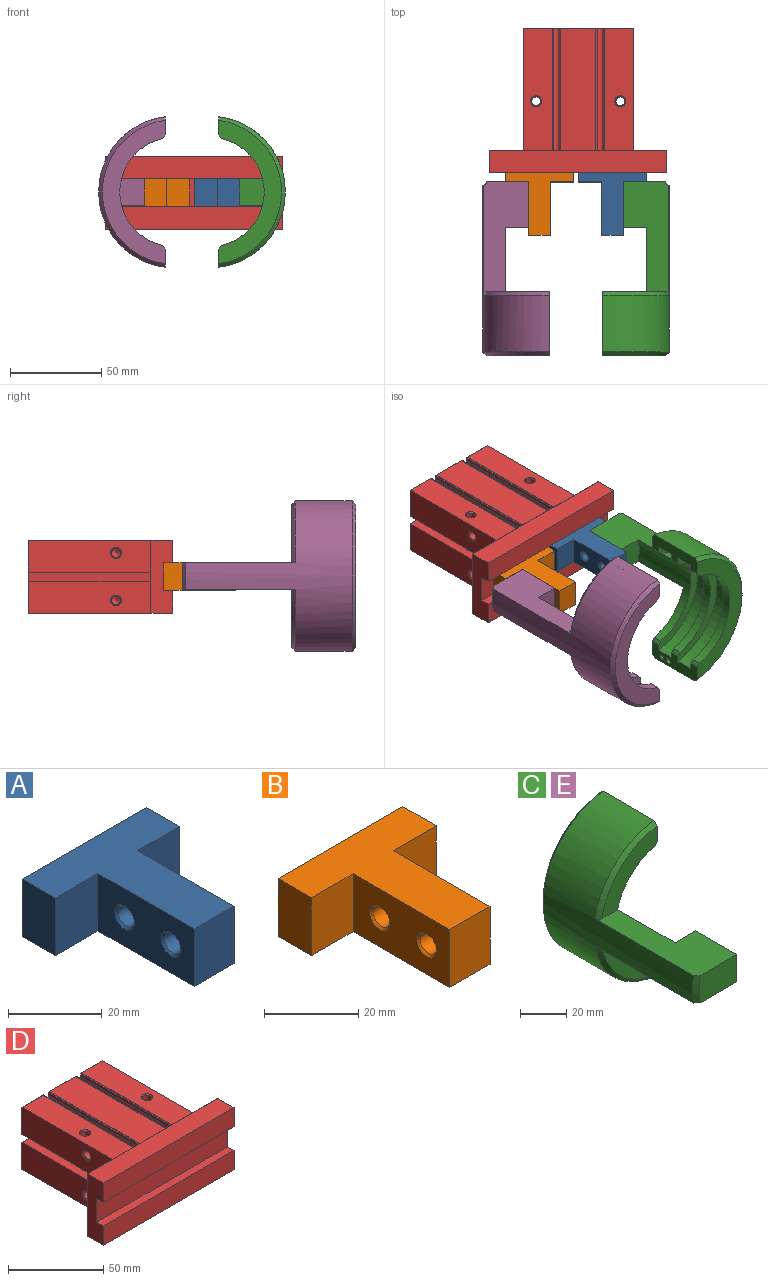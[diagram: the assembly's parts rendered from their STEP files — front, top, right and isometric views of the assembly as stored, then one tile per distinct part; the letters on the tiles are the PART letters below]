
ASSEMBLY  parts=5 mates=10
PART A: 16 faces, bbox 37.4x39x15 mm
  f0: cone r=3.23mm half-angle=45deg, axis (1,0,0), area 13.1mm2, adj f1,f8
  f1: cylinder r=2.46mm len=10.92mm, axis (1,0,0), area 168.8mm2, adj f0,f2
  f2: cone r=3.23mm half-angle=45deg, axis (-1,0,0), area 13.1mm2, adj f1,f6
  f3: cone r=3.23mm half-angle=45deg, axis (1,0,0), area 13.1mm2, adj f4,f8
  f4: cylinder r=2.46mm len=10.92mm, axis (1,0,0), area 168.8mm2, adj f3,f5
  f5: cone r=3.23mm half-angle=45deg, axis (-1,0,0), area 13.1mm2, adj f4,f6
  f6: plane 29x15mm, normal (-1,0,0), area 378.5mm2, adj f2,f5,f7,f13,f14,f15
  f7: plane 15x12mm, normal (0,-1,0), area 180mm2, adj f6,f8,f14,f15
  f8: plane 29x15mm, normal (1,0,0), area 378.5mm2, adj f0,f3,f7,f9,f14,f15
  f9: plane 15x12.5mm, normal (0,-1,0), area 187.5mm2, adj f8,f10,f14,f15
  f10: plane 15x10mm, normal (1,0,0), area 150mm2, adj f9,f11,f14,f15
  f11: plane 37.4x15mm, normal (0,1,0), area 561mm2, adj f10,f12,f14,f15
  f12: plane 15x10mm, normal (-1,0,0), area 150mm2, adj f11,f13,f14,f15
  f13: plane 15x12.9mm, normal (0,-1,0), area 193.5mm2, adj f6,f12,f14,f15
  f14: plane 39x37.4mm, normal (0,0,-1), area 722mm2, adj f6,f7,f8,f9,f10,f11,f12,f13
  f15: plane 39x37.4mm, normal (0,0,1), area 722mm2, adj f6,f7,f8,f9,f10,f11,f12,f13
PART B: 16 faces, bbox 37.4x39x15 mm
  f0: cone r=3.23mm half-angle=45deg, axis (1,0,0), area 13.1mm2, adj f1,f8
  f1: cylinder r=2.46mm len=10.92mm, axis (1,0,0), area 168.8mm2, adj f0,f2
  f2: cone r=3.23mm half-angle=45deg, axis (-1,0,0), area 13.1mm2, adj f1,f6
  f3: cone r=3.23mm half-angle=45deg, axis (1,0,0), area 13.1mm2, adj f4,f8
  f4: cylinder r=2.46mm len=10.92mm, axis (1,0,0), area 168.8mm2, adj f3,f5
  f5: cone r=3.23mm half-angle=45deg, axis (-1,0,0), area 13.1mm2, adj f4,f6
  f6: plane 29x15mm, normal (-1,0,0), area 378.5mm2, adj f2,f5,f7,f13,f14,f15
  f7: plane 15x12mm, normal (0,-1,0), area 180mm2, adj f6,f8,f14,f15
  f8: plane 29x15mm, normal (1,0,0), area 378.5mm2, adj f0,f3,f7,f9,f14,f15
  f9: plane 15x12.9mm, normal (0,-1,0), area 193.5mm2, adj f8,f10,f14,f15
  f10: plane 15x10mm, normal (1,0,0), area 150mm2, adj f9,f11,f14,f15
  f11: plane 37.4x15mm, normal (0,1,0), area 561mm2, adj f10,f12,f14,f15
  f12: plane 15x10mm, normal (-1,0,0), area 150mm2, adj f11,f13,f14,f15
  f13: plane 15x12.5mm, normal (0,-1,0), area 187.5mm2, adj f6,f12,f14,f15
  f14: plane 39x37.4mm, normal (0,0,-1), area 722mm2, adj f6,f7,f8,f9,f10,f11,f12,f13
  f15: plane 39x37.4mm, normal (0,0,1), area 722mm2, adj f6,f7,f8,f9,f10,f11,f12,f13
PART C: 38 faces, bbox 36.7x95x82.4 mm
  f0: plane 25x14.41mm, normal (1,0,0), area 360.3mm2, adj f1,f2,f35,f37
  f1: plane 60.01x24.38mm, normal (0,0,-1), area 1018.4mm2, adj f0,f5,f15,f16,f33,f35,f36,f37
  f2: plane 60.01x24.38mm, normal (0,0,1), area 1018.4mm2, adj f0,f6,f15,f16,f34,f35,f36,f37
  f3: plane 2x1.97mm, normal (0.17,0,0.98), area 2mm2, adj f16,f21,f34
  f4: plane 2x1.97mm, normal (0.17,0,-0.98), area 2mm2, adj f16,f22,f33
  f5: plane 33.84x31.98mm, normal (0,-1,0), area 400.6mm2, adj f1,f8,f15,f19,f22
  f6: plane 33.84x31.98mm, normal (0,-1,0), area 400.6mm2, adj f2,f9,f15,f20,f21
  f7: cylinder r=30mm len=58.55mm, axis (0,1,0), area 405.1mm2, adj f10,f11,f17,f27
  f8: plane 35.01x9.98mm, normal (1,0,0), area 262.6mm2, adj f5,f10,f13,f16,f17,f18,f19,f22
  f9: plane 35.01x9.98mm, normal (1,0,0), area 276.7mm2, adj f6,f11,f14,f16,f17,f18,f20,f21
  f10: plane 5x1.95mm, normal (0.78,0,0.62), area 12.5mm2, adj f7,f8,f17,f27
  f11: plane 5x1.95mm, normal (0.78,0,-0.62), area 12.5mm2, adj f7,f9,f17,f27
  f12: cylinder r=30mm len=58.55mm, axis (0,1,0), area 405.1mm2, adj f13,f14,f24,f28
  f13: plane 5x1.95mm, normal (0.78,0,0.62), area 12.5mm2, adj f8,f12,f24,f28
  f14: plane 5x1.95mm, normal (0.78,0,-0.62), area 12.5mm2, adj f9,f12,f24,f28
  f15: cylinder r=30mm len=58.55mm, axis (0,1,0), area 914.5mm2, adj f1,f2,f5,f6,f19,f20,f25,f37
  f16: cylinder r=41.5mm len=91mm, axis (0,1,0), area 4600.1mm2, adj f1,f2,f3,f4,f8,f9,f18,f21
  f17: plane 78.36x34.5mm, normal (0,1,0), area 939.2mm2, adj f7,f8,f9,f10,f11,f18
  f18: cone r=41.5mm half-angle=45deg, axis (0,-1,0), area 331.5mm2, adj f8,f9,f16,f17
  f19: plane 5x1.95mm, normal (0.78,0,0.62), area 12.5mm2, adj f5,f8,f15,f25
  f20: plane 5x1.95mm, normal (0.78,0,-0.62), area 12.5mm2, adj f6,f9,f15,f25
  f21: cone r=39.5mm half-angle=45deg, axis (0,1,0), area 145.8mm2, adj f3,f6,f9,f16,f34
  f22: cone r=39.5mm half-angle=45deg, axis (0,1,0), area 145.8mm2, adj f4,f5,f8,f16,f33
  f23: cylinder r=35mm len=69.28mm, axis (0,-1,0), area 999.2mm2, adj f8,f9,f24,f25
  f24: plane 69.28x30mm, normal (0,-1,0), area 457.8mm2, adj f8,f9,f12,f13,f14,f23
  f25: plane 69.28x30mm, normal (0,1,0), area 457.8mm2, adj f8,f9,f15,f19,f20,f23
  f26: cylinder r=35mm len=69.28mm, axis (0,-1,0), area 999.2mm2, adj f8,f9,f27,f28
  f27: plane 69.28x30mm, normal (0,-1,0), area 457.8mm2, adj f7,f8,f9,f10,f11,f26
  f28: plane 69.28x30mm, normal (0,1,0), area 457.8mm2, adj f8,f9,f12,f13,f14,f26
  f29: cylinder r=1.5mm len=5mm, axis (1,0,0), area 47.1mm2, adj f8,f30
  f30: plane 3x3mm, normal (1,0,0), area 7.1mm2, adj f29
  f31: cylinder r=1.5mm len=5mm, axis (1,0,0), area 47.1mm2, adj f8,f32
  f32: plane 3x3mm, normal (1,0,0), area 7.1mm2, adj f31
  f33: plane 2.03x0.35mm, normal (0,1,0), area 0.4mm2, adj f1,f4,f22
  f34: plane 2.03x0.35mm, normal (0,1,0), area 0.4mm2, adj f2,f3,f21
  f35: plane 23x14.41mm, normal (0,-1,0), area 328.3mm2, adj f0,f1,f2,f36
  f36: cone r=39.5mm half-angle=45deg, axis (0,1,0), area 41mm2, adj f1,f2,f16,f35
  f37: plane 14.41x13.5mm, normal (0,1,0), area 190.4mm2, adj f0,f1,f2,f15
PART D: 114 faces, bbox 97x79x40 mm
  f0: cylinder r=2.5mm len=5mm, axis (0,-1,0), area 78.5mm2, adj f43,f96
  f1: cone r=1.23mm half-angle=60deg, axis (0,1,0), area 22mm2, adj f2
  f2: cylinder r=2.46mm len=15.46mm, axis (0,-1,0), area 239mm2, adj f1,f3
  f3: cone r=3.23mm half-angle=45deg, axis (0,1,0), area 13.1mm2, adj f2,f43
  f4: cone r=3.23mm half-angle=45deg, axis (0,1,0), area 13.1mm2, adj f5,f43
  f5: cylinder r=2.46mm len=15.46mm, axis (0,1,0), area 239mm2, adj f4,f6
  f6: cone r=1.23mm half-angle=60deg, axis (0,1,0), area 22mm2, adj f5
  f7: cone r=2.87mm half-angle=45deg, axis (1,0,0), area 5.5mm2, adj f8,f46
  f8: cylinder r=2.24mm len=4.74mm, axis (1,0,0), area 66.7mm2, adj f7,f95
  f9: cylinder r=2.24mm len=4.74mm, axis (-1,0,0), area 66.7mm2, adj f10,f94
  f10: cone r=2.87mm half-angle=45deg, axis (1,0,0), area 5.5mm2, adj f9,f46
  f11: cone r=3.23mm half-angle=45deg, axis (0,0,-1), area 13.1mm2, adj f22,f36
  f12: cylinder r=2.46mm len=16.95mm, axis (0,0,-1), area 258.2mm2, adj f13,f54,f55,f56,f60
  f13: cone r=3.23mm half-angle=45deg, axis (0,0,1), area 13.1mm2, adj f12,f50
  f14: cone r=3.23mm half-angle=45deg, axis (0,0,-1), area 13.1mm2, adj f21,f36
  f15: cylinder r=2.46mm len=16.95mm, axis (0,0,-1), area 258.2mm2, adj f16,f45,f63,f67,f68
  f16: cone r=3.23mm half-angle=45deg, axis (0,0,1), area 13.1mm2, adj f15,f50
  f17: cylinder r=2.01mm len=66.8mm, axis (0,-1,0), area 594.2mm2, adj f43,f89,f91,f92
  f18: cylinder r=2.01mm len=66.8mm, axis (0,-1,0), area 594.2mm2, adj f43,f83,f85,f86
  f19: cylinder r=2.01mm len=66.8mm, axis (0,-1,0), area 594.2mm2, adj f43,f78,f80,f81
  f20: cylinder r=2.01mm len=66.8mm, axis (0,-1,0), area 594.2mm2, adj f43,f71,f74,f75
  f21: cylinder r=2.46mm len=16.95mm, axis (0,0,-1), area 258.2mm2, adj f14,f47,f65,f66,f69
  f22: cylinder r=2.46mm len=16.95mm, axis (0,0,-1), area 258.2mm2, adj f11,f57,f58,f59,f61
  f23: cone r=1.23mm half-angle=60deg, axis (-1,0,0), area 22mm2, adj f24
  f24: cylinder r=2.46mm len=10.46mm, axis (1,0,0), area 161.7mm2, adj f23,f25
  f25: cone r=3.23mm half-angle=45deg, axis (-1,0,0), area 13.1mm2, adj f24,f51
  f26: cone r=3.23mm half-angle=45deg, axis (-1,0,0), area 13.1mm2, adj f27,f51
  f27: cylinder r=2.46mm len=10.46mm, axis (-1,0,0), area 161.7mm2, adj f26,f28
  f28: cone r=1.23mm half-angle=60deg, axis (-1,0,0), area 22mm2, adj f27
  f29: cylinder r=17mm len=34mm, axis (0,-1,0), area 427.3mm2, adj f43,f52
  f30: plane 19.3x0.09mm, normal (0,0.71,-0.71), area 2.5mm2, adj f35,f36,f43,f73
  f31: plane 15.65x0.09mm, normal (0,0.71,-0.71), area 2mm2, adj f34,f36,f43,f48
  f32: plane 15.65x0.09mm, normal (0,0.71,-0.71), area 2mm2, adj f33,f36,f43,f77
  f33: plane 17.49x0.09mm, normal (0.71,0.71,0), area 2.2mm2, adj f32,f43,f46,f47
  f34: plane 66.8x0.21mm, normal (1,0,0), area 14mm2, adj f31,f36,f43,f79,f80
  f35: plane 66.8x0.21mm, normal (-1,0,0), area 14mm2, adj f30,f36,f43,f80,f82
  f36: plane 66.91x60mm, normal (0,0,-1), area 3331mm2, adj f11,f14,f30,f31,f32,f34,f35,f46
  f37: plane 19.3x0.09mm, normal (0,0.71,0.71), area 2.5mm2, adj f42,f43,f50,f88
  f38: plane 15.65x0.09mm, normal (0,0.71,0.71), area 2mm2, adj f41,f43,f49,f50
  f39: plane 15.65x0.09mm, normal (0,0.71,0.71), area 2mm2, adj f40,f43,f44,f50
  f40: plane 66.8x0.21mm, normal (-1,0,0), area 14mm2, adj f39,f43,f50,f84,f85
  f41: plane 66.8x0.21mm, normal (1,0,0), area 14mm2, adj f38,f43,f50,f91,f93
  f42: plane 66.8x0.21mm, normal (-1,0,0), area 14mm2, adj f37,f43,f50,f90,f91
  f43: plane 59.82x39.82mm, normal (0,1,0), area 1204.2mm2, adj f0,f3,f4,f17,f18,f19,f20,f29
  f44: plane 17.49x0.09mm, normal (0.71,0.71,0), area 2.2mm2, adj f39,f43,f45,f46
  f45: plane 66.8x7.7mm, normal (0,0,-1), area 501.5mm2, adj f15,f43,f44,f46,f63,f68,f70
  f46: plane 66.91x40mm, normal (1,0,0), area 2302.2mm2, adj f7,f10,f33,f36,f44,f45,f47,f50
  f47: plane 66.8x7.7mm, normal (0,0,1), area 501.5mm2, adj f21,f33,f43,f46,f66,f69,f70
  f48: plane 17.49x0.09mm, normal (-0.71,0.71,0), area 2.2mm2, adj f31,f43,f51,f61
  f49: plane 17.49x0.09mm, normal (-0.71,0.71,0), area 2.2mm2, adj f38,f43,f51,f60
  f50: plane 66.91x60mm, normal (0,0,1), area 3331mm2, adj f13,f16,f37,f38,f39,f40,f41,f42
  f51: plane 66.91x40mm, normal (-1,0,0), area 2285mm2, adj f25,f26,f36,f48,f49,f50,f60,f61
  f52: plane 34x34mm, normal (0,1,0), area 907.9mm2, adj f29
  f53: plane 66.8x6.22mm, normal (-1,0,0), area 415.5mm2, adj f43,f54,f59,f62
  f54: plane 66.8x3.8mm, normal (0,0,-1), area 247.8mm2, adj f12,f43,f53,f55,f56,f62
  f55: plane 24.44x0.6mm, normal (1,0,0), area 14.7mm2, adj f12,f54,f60,f62
  f56: plane 37.64x0.6mm, normal (1,0,0), area 22.6mm2, adj f12,f43,f54,f60
  f57: plane 24.44x0.6mm, normal (1,0,0), area 14.7mm2, adj f22,f59,f61,f62
  f58: plane 37.64x0.6mm, normal (1,0,0), area 22.6mm2, adj f22,f43,f59,f61
  f59: plane 66.8x3.8mm, normal (0,0,1), area 247.8mm2, adj f22,f43,f53,f57,f58,f62
  f60: plane 66.8x7.7mm, normal (0,0,-1), area 501.4mm2, adj f12,f43,f49,f51,f55,f56,f62
  f61: plane 66.8x7.7mm, normal (0,0,1), area 501.4mm2, adj f22,f43,f48,f51,f57,f58,f62
  f62: plane 11.5x6.22mm, normal (0,1,0), area 62.3mm2, adj f51,f53,f54,f55,f57,f59,f60,f61
  f63: plane 24.44x0.6mm, normal (-1,0,0), area 14.7mm2, adj f15,f45,f67,f70
  f64: plane 66.8x6.22mm, normal (1,0,0), area 415.5mm2, adj f43,f65,f67,f70
  f65: plane 66.8x3.8mm, normal (0,0,1), area 247.7mm2, adj f21,f43,f64,f66,f69,f70
  f66: plane 24.44x0.6mm, normal (-1,0,0), area 14.7mm2, adj f21,f47,f65,f70
  f67: plane 66.8x3.8mm, normal (0,0,-1), area 247.7mm2, adj f15,f43,f63,f64,f68,f70
  f68: plane 37.64x0.6mm, normal (-1,0,0), area 22.6mm2, adj f15,f43,f45,f67
  f69: plane 37.64x0.6mm, normal (-1,0,0), area 22.6mm2, adj f21,f43,f47,f65
  f70: plane 11.5x6.22mm, normal (0,1,0), area 62.3mm2, adj f45,f46,f47,f63,f64,f65,f66,f67
  f71: plane 66.8x1.89mm, normal (1,0,0), area 126mm2, adj f20,f43,f72,f74
  f72: plane 66.8x0.74mm, normal (0,0,-1), area 49.4mm2, adj f43,f71,f73,f74
  f73: plane 66.8x0.21mm, normal (1,0,0), area 14mm2, adj f30,f36,f43,f72,f74
  f74: plane 5.31x4.7mm, normal (0,1,0), area 17.9mm2, adj f20,f36,f71,f72,f73,f75,f76,f77
  f75: plane 66.8x1.89mm, normal (-1,0,0), area 126mm2, adj f20,f43,f74,f76
  f76: plane 66.8x0.74mm, normal (0,0,-1), area 49.4mm2, adj f43,f74,f75,f77
  f77: plane 66.8x0.21mm, normal (-1,0,0), area 14mm2, adj f32,f36,f43,f74,f76
  f78: plane 66.8x1.89mm, normal (1,0,0), area 126mm2, adj f19,f43,f79,f80
  f79: plane 66.8x0.74mm, normal (0,0,-1), area 49.4mm2, adj f34,f43,f78,f80
  f80: plane 5.31x4.7mm, normal (0,1,0), area 17.9mm2, adj f19,f34,f35,f36,f78,f79,f81,f82
  f81: plane 66.8x1.89mm, normal (-1,0,0), area 126mm2, adj f19,f43,f80,f82
  f82: plane 66.8x0.74mm, normal (0,0,-1), area 49.4mm2, adj f35,f43,f80,f81
  f83: plane 66.8x1.89mm, normal (-1,0,0), area 126mm2, adj f18,f43,f84,f85
  f84: plane 66.8x0.74mm, normal (0,0,1), area 49.4mm2, adj f40,f43,f83,f85
  f85: plane 5.31x4.7mm, normal (0,1,0), area 17.9mm2, adj f18,f40,f50,f83,f84,f86,f87,f88
  f86: plane 66.8x1.89mm, normal (1,0,0), area 126mm2, adj f18,f43,f85,f87
  f87: plane 66.8x0.74mm, normal (0,0,1), area 49.4mm2, adj f43,f85,f86,f88
  f88: plane 66.8x0.21mm, normal (1,0,0), area 14mm2, adj f37,f43,f50,f85,f87
  f89: plane 66.8x1.89mm, normal (-1,0,0), area 126mm2, adj f17,f43,f90,f91
  f90: plane 66.8x0.74mm, normal (0,0,1), area 49.4mm2, adj f42,f43,f89,f91
  f91: plane 5.31x4.7mm, normal (0,1,0), area 17.9mm2, adj f17,f41,f42,f50,f89,f90,f92,f93
  f92: plane 66.8x1.89mm, normal (1,0,0), area 126mm2, adj f17,f43,f91,f93
  f93: plane 66.8x0.74mm, normal (0,0,1), area 49.4mm2, adj f41,f43,f91,f92
  f94: plane 4.48x4.48mm, normal (1,0,0), area 15.8mm2, adj f9
  f95: plane 4.48x4.48mm, normal (1,0,0), area 15.8mm2, adj f8
  f96: plane 5x5mm, normal (0,1,0), area 19.6mm2, adj f0
  f97: plane 60x0.1mm, normal (0,-1,0), area 6mm2, adj f46,f50,f51,f106
  f98: plane 60x0.1mm, normal (0,-1,0), area 6mm2, adj f36,f46,f51,f102
  f99: plane 39.8x18.4mm, normal (0,1,0), area 732.3mm2, adj f51,f102,f103,f106
  f100: plane 39.8x18.4mm, normal (0,1,0), area 732.3mm2, adj f46,f101,f102,f106
  f101: plane 40x0.1mm, normal (0.71,0.71,0), area 5.6mm2, adj f100,f102,f105,f106
  f102: plane 97x0.1mm, normal (0,0.71,-0.71), area 13.7mm2, adj f98,f99,f100,f101,f103,f104
  f103: plane 40x0.1mm, normal (-0.71,0.71,0), area 5.6mm2, adj f99,f102,f106,f107
  f104: plane 97x11.9mm, normal (0,0,-1), area 1154.3mm2, adj f102,f105,f107,f111
  f105: plane 40x11.9mm, normal (1,0,0), area 401.5mm2, adj f101,f104,f108,f109,f110,f111,f112,f113
  f106: plane 97x0.1mm, normal (0,0.71,0.71), area 13.7mm2, adj f97,f99,f100,f101,f103,f112
  f107: plane 40x11.9mm, normal (-1,0,0), area 401.5mm2, adj f103,f104,f108,f109,f110,f111,f112,f113
  f108: plane 97x4.9mm, normal (0,0,1), area 475.3mm2, adj f105,f107,f109,f111
  f109: plane 97x15.2mm, normal (0,-1,0), area 1474.4mm2, adj f105,f107,f108,f110
  f110: plane 97x4.9mm, normal (0,0,-1), area 475.3mm2, adj f105,f107,f109,f113
  f111: plane 97x12.4mm, normal (0,-1,0), area 1202.8mm2, adj f104,f105,f107,f108
  f112: plane 97x11.9mm, normal (0,0,1), area 1154.3mm2, adj f105,f106,f107,f113
  f113: plane 97x12.4mm, normal (0,-1,0), area 1202.8mm2, adj f105,f107,f110,f112
PART E: same geometry as C
PLACE A t=(80.91,-39.85,9.18)mm
PLACE B rot(axis=(-1,0,0),0deg) t=(78.91,-39.85,9.18)mm
PLACE C rot(axis=(0,0,-1),180deg) t=(89.41,-139.85,9.47)mm
PLACE D t=(81.14,-39.75,9.08)mm
PLACE E rot(axis=(1,0,0),180deg) t=(70.41,-139.85,9.47)mm
MATE planar C.f35 <-> A.f9  axis (0,1,0) through (117.3,-44.85,9.47)mm
MATE planar D.f110 <-> A.f15  axis (0,0,-1) through (81.14,-37.3,16.68)mm
MATE planar E.f1 <-> B.f15  axis (0,0,1) through (39.2,-69.49,16.68)mm
MATE planar A.f11 <-> D.f29  axis (0,1,0) through (99.71,-34.85,9.18)mm
MATE planar B.f15 <-> D.f110  axis (0,0,1) through (60.01,-49.25,16.68)mm
MATE planar E.f35 <-> B.f13  axis (0,1,0) through (42.52,-44.85,9.47)mm
MATE planar B.f11 <-> D.f29  axis (0,1,0) through (60.11,-34.85,9.18)mm
MATE planar C.f0 <-> A.f8  axis (-1,0,0) through (105.91,-57.35,9.47)mm
MATE planar C.f2 <-> A.f15  axis (0,0,1) through (120.62,-69.49,16.68)mm
MATE planar E.f0 <-> B.f6  axis (1,0,0) through (53.91,-57.35,9.47)mm
